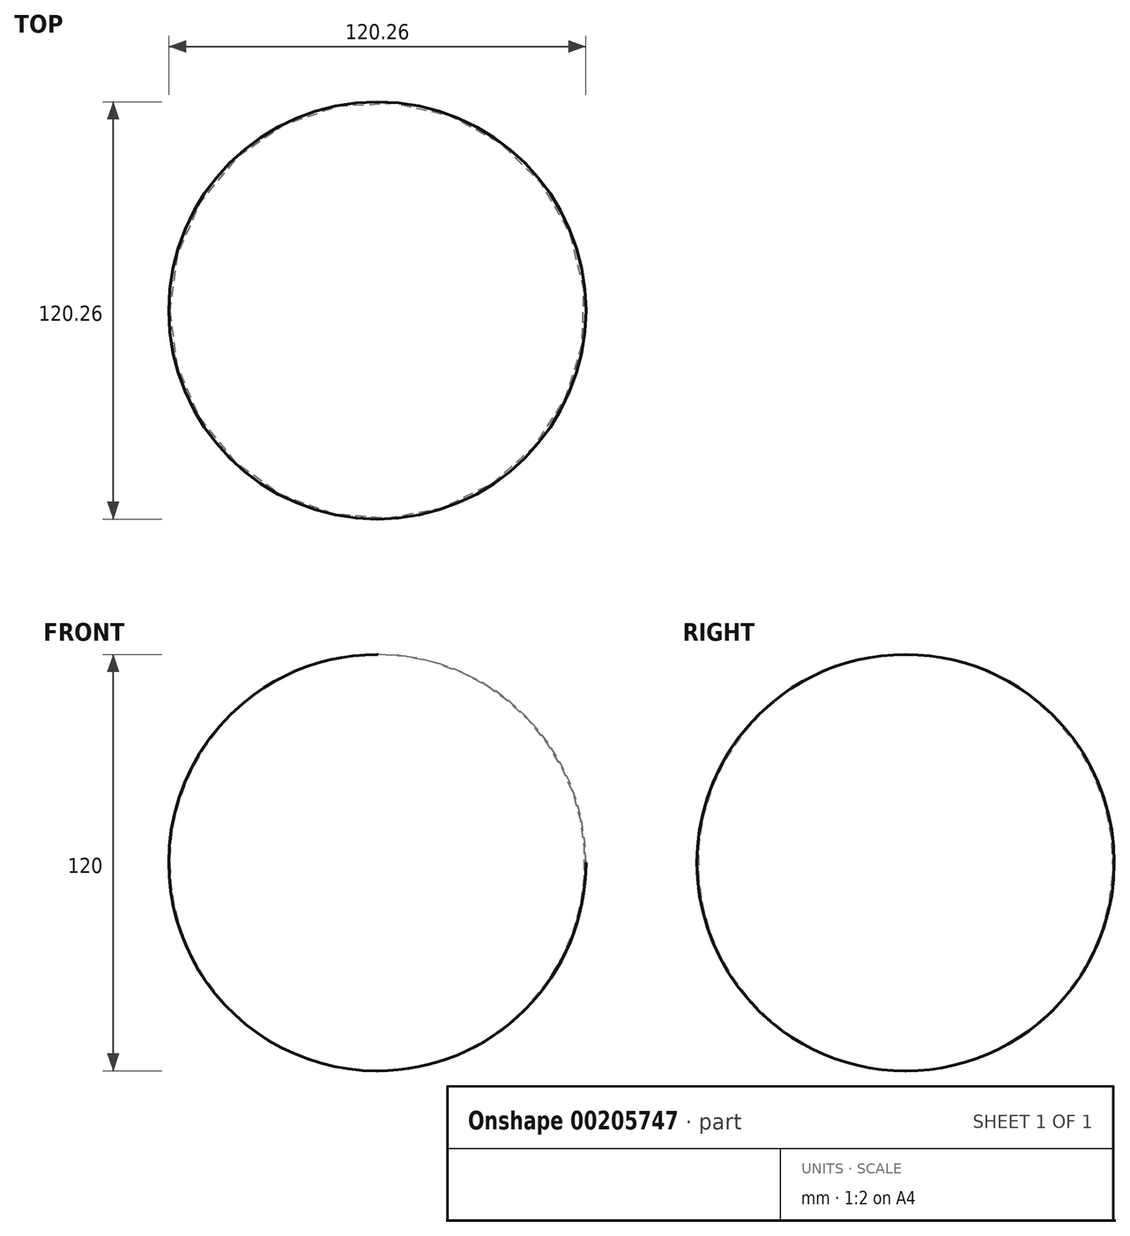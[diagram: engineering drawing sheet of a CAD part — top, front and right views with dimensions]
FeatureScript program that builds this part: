
annotation { "Feature Type Name" : "Feature", "Feature Type Description" : "" }
export const myFeature = defineFeature(function(context is Context, id is Id, definition is map)
    precondition{}
    {
        {
            var Q0;
            Q0=qCreatedBy(makeId("Front.planeOp"),FACE);
            var sketch = newSketch(context, id + "F0", { "sketchPlane" : qUnion([Q0])});
            skLineSegment(sketch, "E0", {"start": v(0, -60) * mm, "end": v(0, 60) * mm});
            skArc(sketch, "E1", {"start": v(0, -60) * mm, "mid": v(60.13, 0) * mm, "end": v(0, 60) * mm});
            skLineSegment(sketch, "E2", {"start": v(0, 75.27) * mm, "end": v(0, -74.73) * mm});
            skSolve(sketch);
        }
        {
            var Q0;
            {var subQ0=sQuery(id+"F0.wireOp",EDGE,"E1");Q0=makeQuery(id+"F0.imprint","IMPRINT",FACE,{"disambiguationData":[TD([[makeQuery(id+"F0.imprint","IMPRINT",EDGE,{"derivedFrom":subQ0}),1.0]])]});}
            var Q1;
            Q1=sQuery(id+"F0.wireOp",EDGE,"E2");
            revolve(context, id + "F1", {"entities" : qUnion([Q0]), "axis" : qUnion([Q1]), "revolveType" : RevolveType.FULL});
        }
    });
